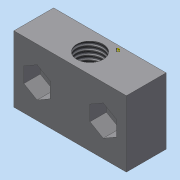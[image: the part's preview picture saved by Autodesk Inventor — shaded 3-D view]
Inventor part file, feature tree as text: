
AUTODESK INVENTOR PART (.ipt)
format: ipt  version: 2013 SP2 (Build 170200200, 200)  size: 125,440 bytes
history: native  units: mm
features: sketch x4, extrude x3, hole x1, plane x1, mirror x1, thread x1
ambient origin geometry x8: Origin, YZ Plane, XZ Plane, XY Plane, X Axis, Y Axis, Z Axis, Center Point
bodies: Solid1 (feature_tree)
feature tree (11):
  extrude  "Extrusion1"  Depth=20.0mm
  hole  "Hole1"  [1 undecoded]
  extrude  "Extrusion3"  Depth=10.0mm
  extrude  "Extrusion4"  Depth=9.24mm
  plane  "Work Plane1"
  mirror  "Mirror1"
  thread  "Thread1"  [1 undecoded]
  sketch  "Sketch1"  dims[d0=34.0mm d1=20.0mm]
  sketch  "Sketch2"  dims[d2=12.0mm d3=0.0mm d4=7.0mm]
  sketch  "Sketch3"  dims[d5=20.0mm d6=10.0mm]
  sketch  "Sketch4"  dims[d7=5.05mm d8=6.0mm d9=9.0mm d10=1.6mm d11=90.0deg d12=8.0mm d13=20.594885mm d14=9.24mm d17=4.97mm d18=0.0mm d19=8.0mm d21=4.97mm d22=0.0mm d23=17.0mm d24=6.0mm d25=10.0mm d26=0.0mm]
note: 2 required parameter values undecoded (feature->parameter linkage not recoverable at this tier; creation-order binding heuristic only, values carry confidence <= 0.55)
